# Revit family: NLRS_90_SI_Fietsenrek-FalcoSound_Enkelzijdig_flc_FLC
name_source: partatom
category: Site
units: mm (PartAtom-declared; Revit-internal decimal feet)

## family parameters
Always vertical = Yes
Cut with Voids When Loaded = No
Part Type = Normal
Round Connector Dimension = Use Diameter
Shared = No
Work Plane-Based = No

## types (15) — shared parameters
Achterkant fiets = 1557 mm  [stored 5.10827 ft]
Looppad = 3057 mm  [stored 10.0295 ft]
Muur = 374 mm  [stored 1.22703 ft]
NLRS_C_diepte = 400 mm  [stored 1.31234 ft]
NLRS_C_leverancier = Falco B.V.
NLRS_C_leverancier_url = www.falco.nl
NLRS_C_omschrijving = FalcoSound fietsenrek

## per-type parameters (varying)
| type | Assembly Code | Benodigde_Ruimte | Manufacturer | Model | NLRS_C_artikel_code | NLRS_C_lengte | NLRS_C_lengte_01 | NLRS_C_lengte_02 | NLRS_C_lengte_03 | aantal klemmen hoog | aantal klemmen laag | aantal_plaatsen | hartafstand | hoh_dubbel |
| Sound enkelzijdig hoh 375 6 plaatsen l=2250 |  | Yes | Falco BV |  | 00.106.037 | 2250 mm | 188 mm | 1500 mm  [stored 4.92126 ft] | 1500 mm  [stored 4.92126 ft] | 3 | 3 | 6 | 375 mm  [stored 1.23031 ft] | 750 mm  [stored 2.46063 ft] |
| Sound enkelzijdig hoh 375 4 plaatsen l=1500 |  | No | Falco BV |  | 00.104.037 | 1500 mm  [stored 4.92126 ft] | 188 mm | 750 mm  [stored 2.46063 ft] | 750 mm  [stored 2.46063 ft] | 2 | 2 | 4 | 375 mm  [stored 1.23031 ft] | 750 mm  [stored 2.46063 ft] |
| Sound enkelzijdig hoh 375 5 plaatsen l=1875 |  | Yes | Falco BV |  | 00.105.037 | 1875 mm  [stored 6.15157 ft] | 188 mm | 1500 mm  [stored 4.92126 ft] | 750 mm  [stored 2.46063 ft] | 2 | 3 | 5 | 375 mm  [stored 1.23031 ft] | 750 mm  [stored 2.46063 ft] |
| Sound enkelzijdig hoh 375 7 plaatsen l=2625 |  | Yes | Falco BV |  | 00.107.037 | 2625 mm  [stored 8.6122 ft] | 188 mm | 2250 mm | 1500 mm  [stored 4.92126 ft] | 3 | 4 | 7 | 375 mm  [stored 1.23031 ft] | 750 mm  [stored 2.46063 ft] |
| Sound enkelzijdig hoh 375 8 plaatsen l=3000 |  | Yes | Falco BV |  | 00.108.037 | 3000 mm  [stored 9.84252 ft] | 188 mm | 2250 mm | 2250 mm | 4 | 4 | 8 | 375 mm  [stored 1.23031 ft] | 750 mm  [stored 2.46063 ft] |
| Sound enkelzijdig hoh 400 4 plaatsen l=1600 |  | Yes | Falco BV |  | 00.104.040 | 1600 mm  [stored 5.24934 ft] | 200 mm  [stored 0.656168 ft] | 800 mm  [stored 2.62467 ft] | 800 mm  [stored 2.62467 ft] | 2 | 2 | 4 | 400 mm  [stored 1.31234 ft] | 800 mm  [stored 2.62467 ft] |
| Sound enkelzijdig hoh 400 5 plaatsen l=2000 |  | Yes | Falco BV |  | 00.105.040 | 2000 mm  [stored 6.56168 ft] | 200 mm  [stored 0.656168 ft] | 1600 mm  [stored 5.24934 ft] | 800 mm  [stored 2.62467 ft] | 2 | 3 | 5 | 400 mm  [stored 1.31234 ft] | 800 mm  [stored 2.62467 ft] |
| Sound enkelzijdig hoh 400 6 plaatsen l=2400 |  | Yes | Falco BV |  | 00.106.040 | 2400 mm | 200 mm  [stored 0.656168 ft] | 1600 mm  [stored 5.24934 ft] | 1600 mm  [stored 5.24934 ft] | 3 | 3 | 6 | 400 mm  [stored 1.31234 ft] | 800 mm  [stored 2.62467 ft] |
| Sound enkelzijdig hoh 500 4 plaatsen l=2000 |  | Yes | Falco BV |  | 00.104.050 | 2000 mm  [stored 6.56168 ft] | 250 mm  [stored 0.82021 ft] | 1000 mm  [stored 3.28084 ft] | 1000 mm  [stored 3.28084 ft] | 2 | 2 | 4 | 500 mm  [stored 1.64042 ft] | 1000 mm  [stored 3.28084 ft] |
| Sound enkelzijdig hoh 500 5 plaatsen l=2500 |  | Yes | Falco BV |  | 00.105.050 | 2500 mm  [stored 8.2021 ft] | 250 mm  [stored 0.82021 ft] | 2000 mm  [stored 6.56168 ft] | 1000 mm  [stored 3.28084 ft] | 2 | 3 | 5 | 500 mm  [stored 1.64042 ft] | 1000 mm  [stored 3.28084 ft] |
| Sound enkelzijdig hoh 500 6 plaatsen l=3000 | 90.71 | Yes | Falco B.V. | FalcoSound fietsenrek, enkelzijdig | 00.106.050 | 3000 mm  [stored 9.84252 ft] | 250 mm  [stored 0.82021 ft] | 2000 mm  [stored 6.56168 ft] | 2000 mm  [stored 6.56168 ft] | 3 | 3 | 6 | 500 mm  [stored 1.64042 ft] | 1000 mm  [stored 3.28084 ft] |
| Sound enkelzijdig hoh 375 3 plaatsen l=1125 |  | Yes | Falco BV |  | 00.103.037 | 1125 mm | 188 mm | 750 mm  [stored 2.46063 ft] | 750 mm  [stored 2.46063 ft] | 2 | 2 | 3 | 375 mm  [stored 1.23031 ft] | 750 mm  [stored 2.46063 ft] |
| Sound enkelzijdig hoh 400 2 plaatsen l=800 |  | Yes | Falco BV |  | 00.102.040 | 800 mm  [stored 2.62467 ft] | 200 mm  [stored 0.656168 ft] | 800 mm  [stored 2.62467 ft] | 800 mm  [stored 2.62467 ft] | 2 | 2 | 2 | 400 mm  [stored 1.31234 ft] | 800 mm  [stored 2.62467 ft] |
| Sound enkelzijdig hoh 400 3 plaatsen l=1200 |  | Yes | Falco BV |  | 00.103.040 | 1200 mm | 200 mm  [stored 0.656168 ft] | 800 mm  [stored 2.62467 ft] | 800 mm  [stored 2.62467 ft] | 2 | 2 | 3 | 400 mm  [stored 1.31234 ft] | 800 mm  [stored 2.62467 ft] |
| Sound enkelzijdig hoh 375 2 plaatsen l=750 |  | No | Falco BV |  | 00.102.037 | 750 mm  [stored 2.46063 ft] | 188 mm | 750 mm  [stored 2.46063 ft] | 750 mm  [stored 2.46063 ft] | 2 | 2 | 2 | 375 mm  [stored 1.23031 ft] | 750 mm  [stored 2.46063 ft] |

note: [stored X ft] marks values corroborated as IEEE doubles in the binary element streams (Revit-internal decimal feet)

## geometry (parser evidence)
native form markers: Sweep x7
no freeform markers — native parametric forms only
